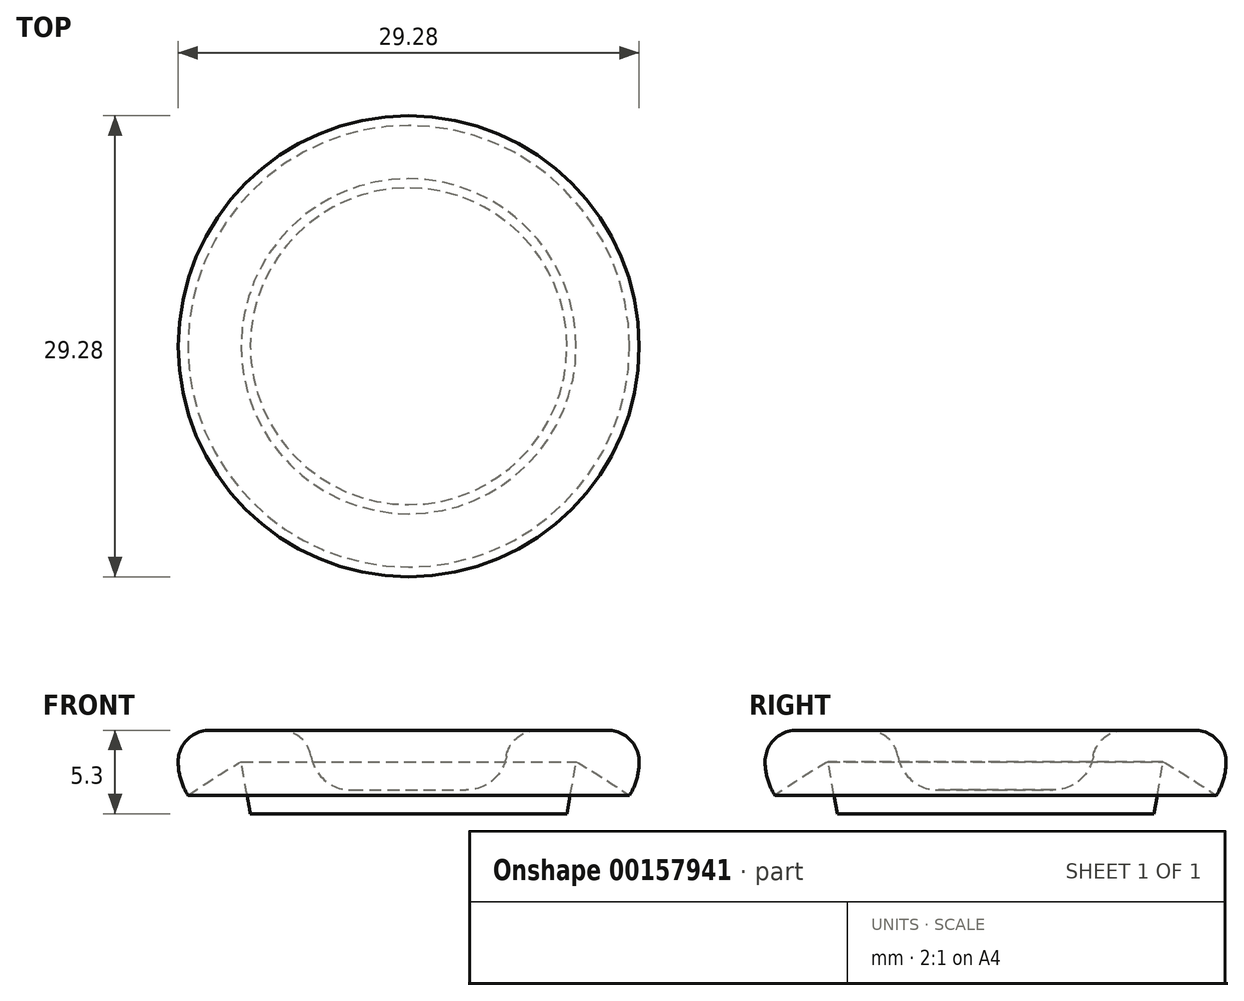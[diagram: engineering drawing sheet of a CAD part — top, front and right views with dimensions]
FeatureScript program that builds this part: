
annotation { "Feature Type Name" : "Feature", "Feature Type Description" : "" }
export const myFeature = defineFeature(function(context is Context, id is Id, definition is map)
    precondition{}
    {
        {
            var Q0;
            Q0=qCreatedBy(makeId("Front.planeOp"),FACE);
            var sketch = newSketch(context, id + "F0", { "sketchPlane" : qUnion([Q0])});
            skLineSegment(sketch, "E0.left", {"start": v(0, 0) * mm, "end": v(0, 0) * mm});
            skLineSegment(sketch, "E1", {"start": v(4.14, 0) * mm, "end": v(4.72, 3.3) * mm});
            skArc(sketch, "E2", {"start": v(4.72, 3.3) * mm, "mid": v(6.43, 2.27) * mm, "end": v(8.1, 1.16) * mm});
            skArc(sketch, "E3", {"start": v(8.1, 1.16) * mm, "mid": v(8.56, 2.19) * mm, "end": v(8.72, 3.3) * mm});
            skLineSegment(sketch, "E4", {"start": v(2.25, 5.3) * mm, "end": v(6.72, 5.3) * mm});
            skArc(sketch, "E5", {"start": v(6.72, 5.3) * mm, "mid": v(8.14, 4.71) * mm, "end": v(8.72, 3.3) * mm});
            skArc(sketch, "E6", {"start": v(2.25, 5.3) * mm, "mid": v(0.97, 4.83) * mm, "end": v(0.28, 3.65) * mm});
            skArc(sketch, "E7", {"start": v(0.28, 3.65) * mm, "mid": v(-0.6, 2.1) * mm, "end": v(-2.28, 1.5) * mm});
            skLineSegment(sketch, "E8", {"start": v(-5.92, 0) * mm, "end": v(-5.92, 1.5) * mm});
            skLineSegment(sketch, "E9", {"start": v(-5.92, 1.5) * mm, "end": v(-2.28, 1.5) * mm});
            skLineSegment(sketch, "E10", {"start": v(-5.92, 0) * mm, "end": v(4.14, 0) * mm});
            skSolve(sketch);
        }
        {
            var Q0;
            Q0=makeQuery(id+"F0.imprint","IMPRINT",FACE,{"disambiguationData":[TD([[makeQuery(id+"F0.imprint","IMPRINT",EDGE,{"derivedFrom":sQuery(id+"F0.wireOp",EDGE,"E1")}),1.0]])]});
            var Q1;
            Q1=sQuery(id+"F0.wireOp",EDGE,"E8");
            revolve(context, id + "F1", {"entities" : qUnion([Q0]), "axis" : qUnion([Q1]), "revolveType" : RevolveType.FULL});
        }
    });
